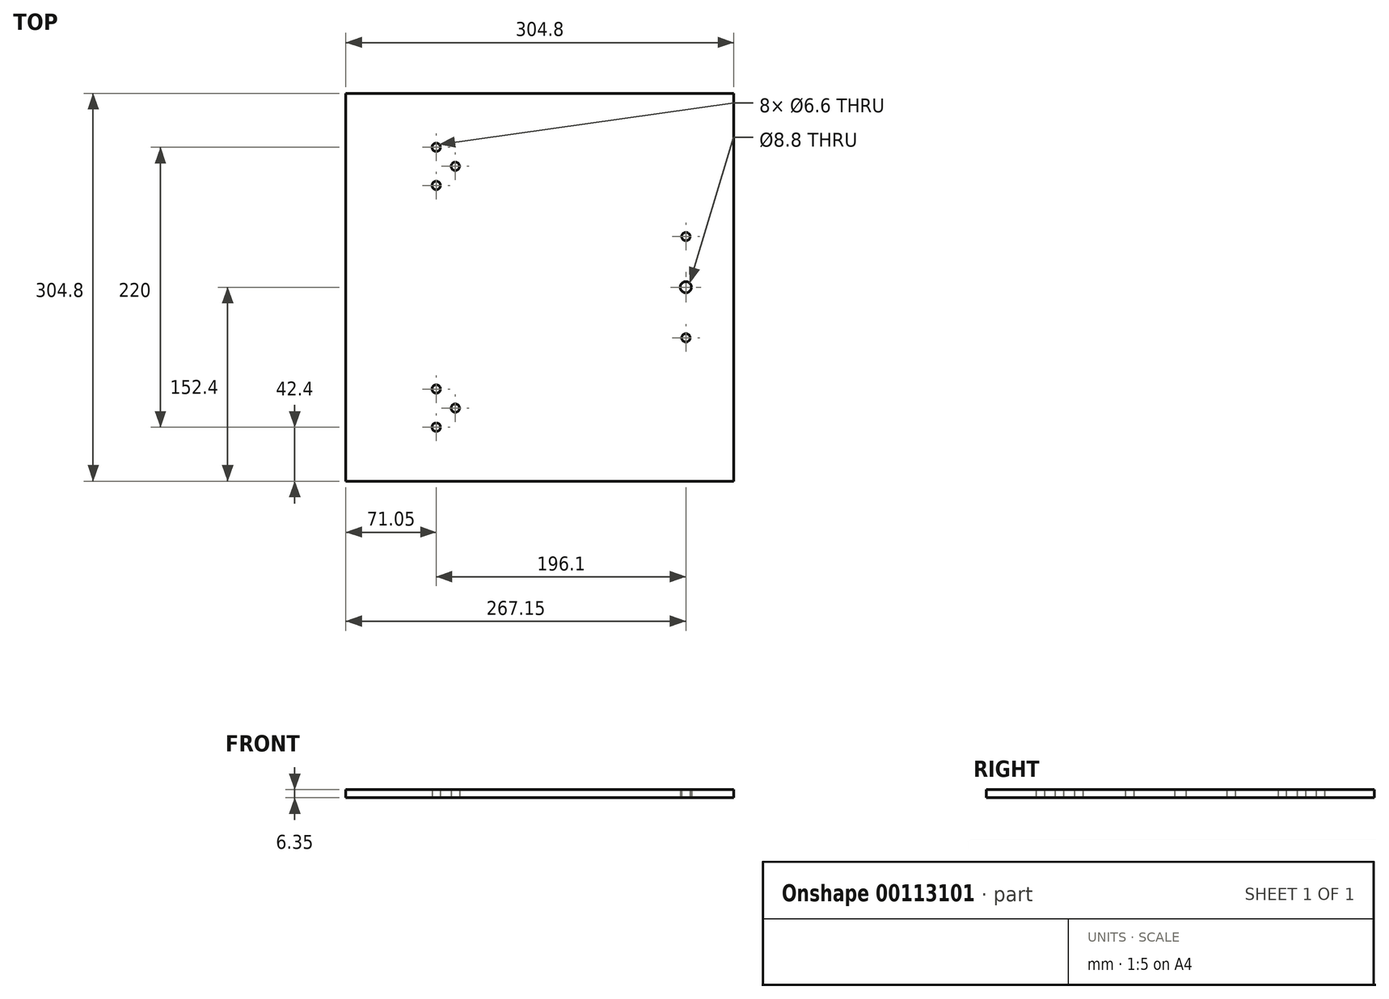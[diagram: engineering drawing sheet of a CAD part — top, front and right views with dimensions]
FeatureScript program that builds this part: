
annotation { "Feature Type Name" : "Feature", "Feature Type Description" : "" }
export const myFeature = defineFeature(function(context is Context, id is Id, definition is map)
    precondition{}
    {
        {
            var Q0;
            Q0=qCreatedBy(makeId("Top.planeOp"),FACE);
            var sketch = newSketch(context, id + "F0", { "sketchPlane" : qUnion([Q0])});
            skLineSegment(sketch, "E0.bottom", {"start": v(152.4, -152.4) * mm, "end": v(-152.4, -152.4) * mm});
            skLineSegment(sketch, "E0.top", {"start": v(152.4, 152.4) * mm, "end": v(-152.4, 152.4) * mm});
            skLineSegment(sketch, "E0.left", {"start": v(152.4, -152.4) * mm, "end": v(152.4, 152.4) * mm});
            skLineSegment(sketch, "E0.right", {"start": v(-152.4, -152.4) * mm, "end": v(-152.4, 152.4) * mm});
            skPoint(sketch, "E0.middle", {"position": v(0, 0) * mm});
            skSolve(sketch);
        }
        {
            var Q0;
            Q0 = qSketchRegion(id + "F0", true);
            extrude(context, id + "F1", {"entities" : qUnion([Q0]), "depth" : 6.35 * mm});
        }
        {
            var Q0;
            Q0=makeQuery(id+"F1.opExtrude","CAP_FACE",FACE,{"disambiguationData":[OSD([sQuery(id+"F0.wireOp",EDGE,"E0.bottom"),sQuery(id+"F0.wireOp",EDGE,"E0.top"),sQuery(id+"F0.wireOp",EDGE,"E0.left"),sQuery(id+"F0.wireOp",EDGE,"E0.right")])],"isStart":false});
            var sketch = newSketch(context, id + "F2", { "sketchPlane" : qUnion([Q0])});
            skPoint(sketch, "E1", {"position": v(-81.35, 80) * mm});
            skPoint(sketch, "E2", {"position": v(-66.35, 95) * mm});
            skPoint(sketch, "E3", {"position": v(-81.35, 110) * mm});
            skPoint(sketch, "E4", {"position": v(114.75, 39.77) * mm});
            skPoint(sketch, "E5.MirrorP", {"position": v(-81.35, -80) * mm});
            skPoint(sketch, "E6.MirrorP", {"position": v(-81.35, -110) * mm});
            skPoint(sketch, "E7.MirrorP", {"position": v(-66.35, -95) * mm});
            skPoint(sketch, "E8.MirrorP", {"position": v(114.75, -39.77) * mm});
            skPoint(sketch, "E9", {"position": v(114.75, 0) * mm});
            skPoint(sketch, "E10.orphan", {"position": v(0, 0) * mm});
            skSolve(sketch);
        }
        {
            var Q0;
            Q0=sQuery(id+"F2.wireOp",VERTEX,"E6.MirrorP");
            var Q1;
            Q1=sQuery(id+"F2.wireOp",VERTEX,"E7.MirrorP");
            var Q2;
            Q2=sQuery(id+"F2.wireOp",VERTEX,"E5.MirrorP");
            var Q3;
            Q3=sQuery(id+"F2.wireOp",VERTEX,"E1");
            var Q4;
            Q4=sQuery(id+"F2.wireOp",VERTEX,"E2");
            var Q5;
            Q5=sQuery(id+"F2.wireOp",VERTEX,"E3");
            var Q6;
            Q6=sQuery(id+"F2.wireOp",VERTEX,"E4");
            var Q7;
            Q7=sQuery(id+"F2.wireOp",VERTEX,"E8.MirrorP");
            var Q8;
            Q8=makeQuery(id+"F1.opExtrude","SWEPT_BODY",BODY,{"disambiguationData":[OSD([sQuery(id+"F0.wireOp",EDGE,"E0.bottom"),sQuery(id+"F0.wireOp",EDGE,"E0.top"),sQuery(id+"F0.wireOp",EDGE,"E0.left"),sQuery(id+"F0.wireOp",EDGE,"E0.right")])]});
            hole(context, id + "F3", {"style" : HoleStyle.SIMPLE, "endStyle" : HoleEndStyle.THROUGH, "standardTappedOrClearance" : lookupTablePath({ "standard" : "ISO", "fit" : "Normal", "size" : "M6", "type" : "Clearance" }), "standardBlindInLast" : lookupTablePath({ "fit" : "Standard", "standard" : "ISO", "size" : "M6", "type" : "Clearance" }), "holeDiameter" : 6.6 * mm, "locations" : qUnion([Q0, Q1, Q2, Q3, Q4, Q5, Q6, Q7]), "scope" : qUnion([Q8]), "isTappedThrough" : true, "startStyle" : HoleStartStyle.SKETCH});
        }
        {
            var Q0;
            Q0=sQuery(id+"F2.wireOp",VERTEX,"E9");
            var Q1;
            Q1=makeQuery(id+"F1.opExtrude","SWEPT_BODY",BODY,{"disambiguationData":[OSD([sQuery(id+"F0.wireOp",EDGE,"E0.bottom"),sQuery(id+"F0.wireOp",EDGE,"E0.top"),sQuery(id+"F0.wireOp",EDGE,"E0.left"),sQuery(id+"F0.wireOp",EDGE,"E0.right")])]});
            hole(context, id + "F4", {"style" : HoleStyle.SIMPLE, "endStyle" : HoleEndStyle.THROUGH, "standardTappedOrClearance" : lookupTablePath({ "standard" : "ISO", "fit" : "Normal", "size" : "M8", "type" : "Clearance" }), "standardBlindInLast" : lookupTablePath({ "fit" : "Standard", "standard" : "ISO", "size" : "M8", "type" : "Clearance" }), "holeDiameter" : 8.8 * mm, "locations" : qUnion([Q0]), "scope" : qUnion([Q1]), "isTappedThrough" : true, "startStyle" : HoleStartStyle.SKETCH});
        }
    });
